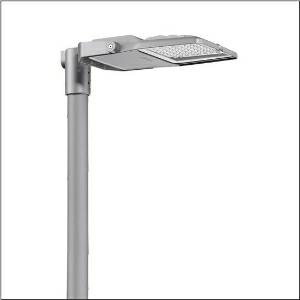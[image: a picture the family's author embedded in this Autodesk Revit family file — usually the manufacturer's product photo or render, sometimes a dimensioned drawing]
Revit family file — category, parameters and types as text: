
# Revit family: floodlight_fl_21_iq_mini___pl61_5xa7771b2c3a_a4a3
name_source: partatom
category: Lighting Fixtures
units: mm (PartAtom-declared; Revit-internal decimal feet)

## family parameters
Cut with Voids When Loaded = No
Host = Face
Light Source = No
Part Type = Normal
Room Calculation Point = No
Round Connector Dimension = Use Diameter
Shared = No

## types (1)
- --- (1 x LED, 6120 lm, 45.5 W, 3000K)
    Apparent Load = 46 VA
    CIE Flux Codes = 33 65 98 100 100
    Color Rendering = 70
    Color Temperature = 3000K
    Default Elevation = 1800 mm
    Description = Floodlight FL 21 iQ mini, floodlight, primary light control with lens, of PMMA, primary optical cover: protective disc, of toughened safety glass, transparent, light distribution: PL61, light emission: direct distribution, installation type: surface-mounted, lamps: LED, High Power LED, rated values: 6.120lm | 45,5W | 134,5lm/W (begin service life); end service life: 6.120lm | 48W; at 50% lumin. flux: 3.060lm | 21,5W | 142,3lm/W, colour temperature: 3000K, colour rendering: CRI > 70, light colour: 730, light setting 1 begin service life: 100% | 6.120lm | 45,5W | 134,5lm/W | 3.000K, light setting 1 end service life: 48W, further light settings possible, control: Auto-Match, Temp-Guard, Lumen-Switch, Night-Set, Smart-Wire, Light-Fading, Desk-Remote (wireless, voltage-free reading and setting of iQ features in the workshop via application-optimized NFC function/RFID function), optimised constant luminous flux control (CLO 2.0), pre-setting: linear dimming characteristic, with terminal, 6-pole, mains connection: 220..240V, AC, 50/60Hz, luminaire housing, of diecast aluminium, powder-coated, SITECO metallic grey (DB 702S), corrosivity category C5 mid according to DIN EN ISO 12944suitable for swimming poolschlorine-resistant, sealing non-destructively replaceable, please order mast flange separately, mast bracket, of steel, galvanised, powder-coated, SITECO metallic grey (DB 702S), protection rating (complete): IP66, insulation class (complete): insulation class II (safety insulation), certification: CE, ENEC, VDE, protection symbol: D, impact resistance: IK08, permissible operating ambient temperature: -40..+40°C, permissible operating ambient temperature for outdoor applications: -40..+50°C, standard: DIN EN 12944, LABS conformity tested according to VDMA 24364:2018-05, packaging unit: 1 piece

Light Distribution: PL61
    Height = 70 mm
    Lamp = 1 x LED
    Lamp Light Flux = 6120 lm
    Lamp Power = 45.5 W
    Lamp count = 1
    Length = 485 mm
    Luminous efficacy = 135 lm/W
    Manufacturer = Siteco
    ModVariant = No
    Model = 5XA7771B2C3A
    Number of Poles = 1
    OnlyDefault = Yes
    Power Factor = 1
    Product Name = Floodlight FL 21 iQ mini | PL61
    Product group = floodlight | pylon annexe
    ProductGroupID = 6201
    Protection Class = Protection class II
    Protection Degree = IP 66
    RLX_Detail_Level = 1
    RLX_Emergency_Light_Flux = 0 lm
    RLX_Emergency_Type = 0
    RLX_Emergency_Type_DB = No
    RlxData = <blob elided: 101537 chars, md5=9c86a9dd>
    Socket = socket
    Standby Power = 0 W
    System Light Flux = 6120 lm
    System Power = 46 W
    Type Comments = factory setting: luminous flux: 100 % | dim-lin: 254 | 463 mA
    Type Image = l_1007125.jpg
    URL = http://relux.com
    VarID = @adj_173321
    Voltage = 0 V
    Weight = 0.00 kg
    Width = 337 mm

## geometry (parser evidence)
native form markers: Blend x4, Sweep x13
no freeform markers — native parametric forms only
